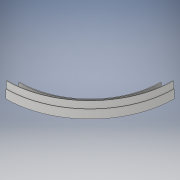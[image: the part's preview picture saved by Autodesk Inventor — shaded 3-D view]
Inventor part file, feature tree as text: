
AUTODESK INVENTOR PART (.ipt)
format: ipt  version: 2017 (Build 210142000, 142)  size: 135,680 bytes
history: native  units: in
note: dims shown in document units (in); Inventor stores cm internally (conversion verified against a paired STEP export)
features: revolve x1, sketch x1
ambient origin geometry x8: Origin, YZ Plane, XZ Plane, XY Plane, X Axis, Y Axis, Z Axis, Center Point
bodies: Solid1 (feature_tree)
feature tree (2):
  revolve  "Revolution1"  [1 undecoded]
  sketch  "Sketch1"  dims[d1=0.9911in d2=5.1195in d4=0.0in d5=0.0625in d6=0.0625in d7=0.0625in d8=0.0625in d9=0.7182in d10=0.3125in d11=0.1562in d12=90.0deg d13=0.8745in d14=0.0312in d15=0.25in d16=0.25in]
note: 1 required parameter value undecoded (feature->parameter linkage not recoverable at this tier; creation-order binding heuristic only, values carry confidence <= 0.55)
